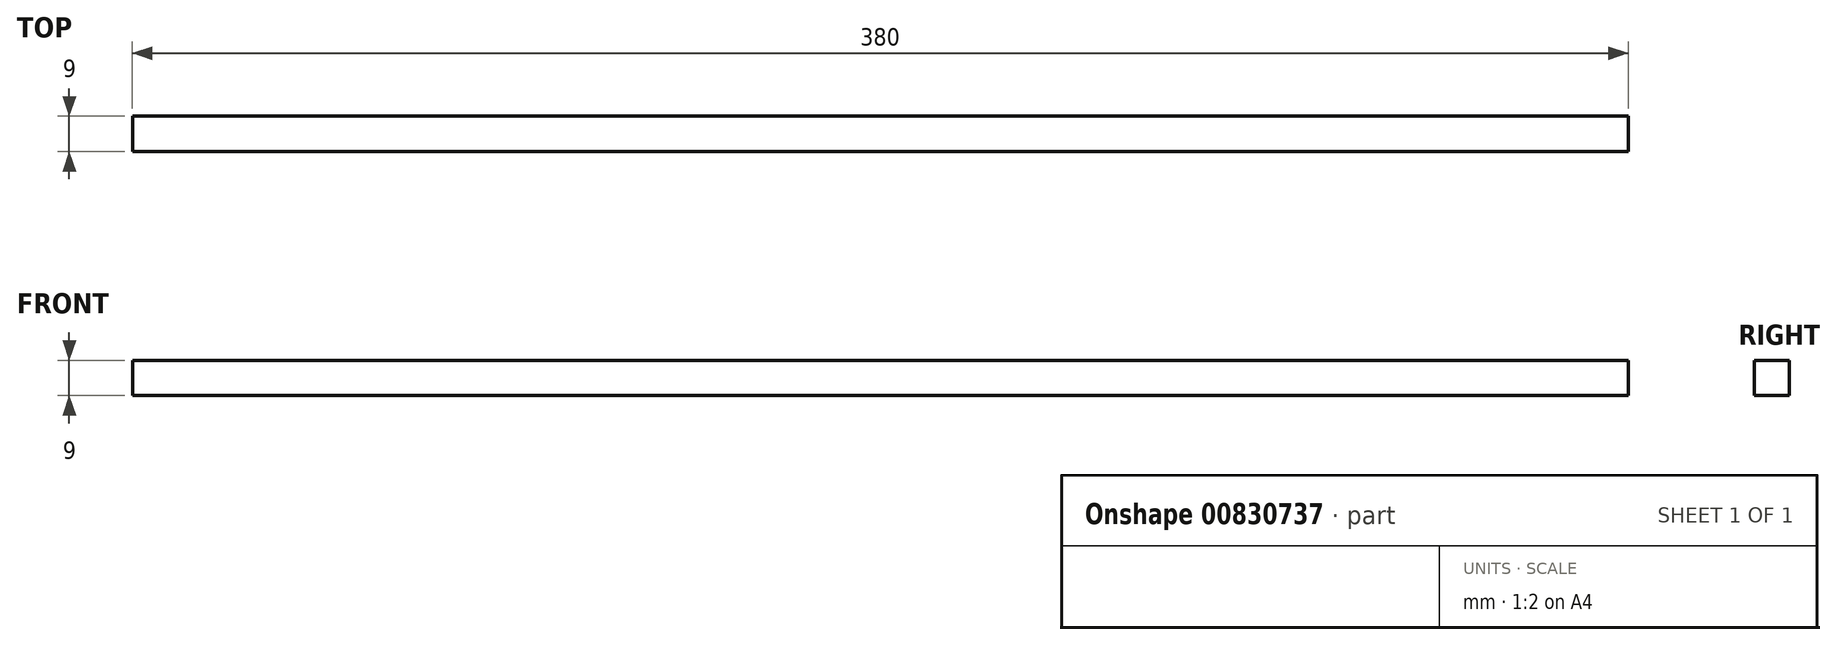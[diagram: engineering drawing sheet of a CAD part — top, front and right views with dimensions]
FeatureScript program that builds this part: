
annotation { "Feature Type Name" : "Feature", "Feature Type Description" : "" }
export const myFeature = defineFeature(function(context is Context, id is Id, definition is map)
    precondition{}
    {
        {
            var Q0;
            Q0=qCreatedBy(makeId("Top.planeOp"),FACE);
            var sketch = newSketch(context, id + "F0", { "sketchPlane" : qUnion([Q0])});
            skLineSegment(sketch, "E0.bottom", {"start": v(-8.79, -7.43) * mm, "end": v(371.21, -7.43) * mm});
            skLineSegment(sketch, "E0.top", {"start": v(-8.79, -16.43) * mm, "end": v(371.21, -16.43) * mm});
            skLineSegment(sketch, "E0.left", {"start": v(-8.79, -7.43) * mm, "end": v(-8.79, -16.43) * mm});
            skLineSegment(sketch, "E0.right", {"start": v(371.21, -7.43) * mm, "end": v(371.21, -16.43) * mm});
            skSolve(sketch);
        }
        {
            var Q0;
            Q0=makeQuery(id+"F0.imprint","IMPRINT",FACE,{"disambiguationData":[TD([[makeQuery(id+"F0.imprint","IMPRINT",EDGE,{"derivedFrom":sQuery(id+"F0.wireOp",EDGE,"E0.bottom")}),-1.0]])]});
            extrude(context, id + "F1", {"entities" : qUnion([Q0]), "depth" : 9 * mm, "offsetDistance" : 25 * mm});
        }
    });
